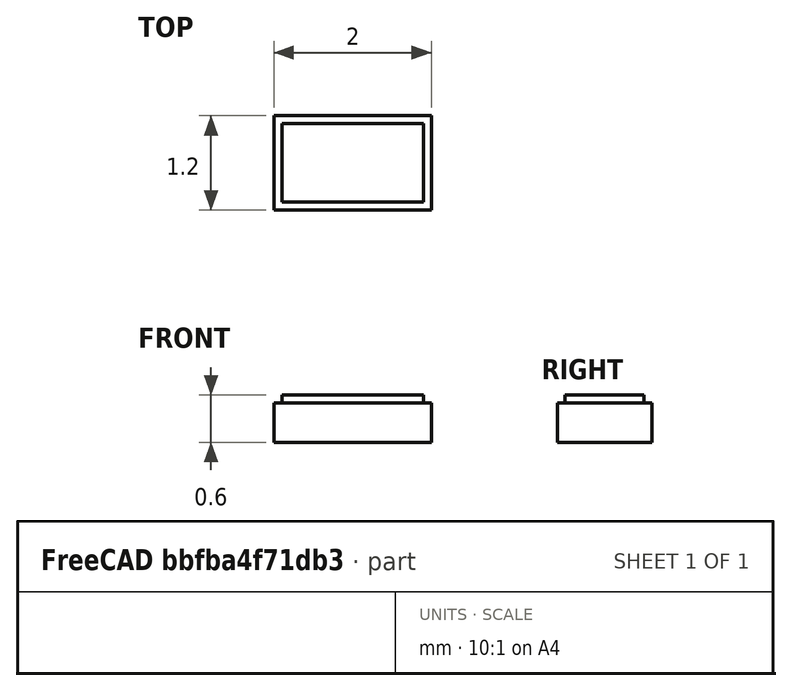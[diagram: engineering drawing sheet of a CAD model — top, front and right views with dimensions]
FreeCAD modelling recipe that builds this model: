
FCSTD DOCUMENT  (FreeCAD 0.16R6712 (Git))
Label: CRYSTAL-ABS06
License: All rights reserved
LicenseURL: http://en.wikipedia.org/wiki/All_rights_reserved
objects: Sketcher::SketchObject×2, PartDesign::Pad×2
note: 6 computed .brp shape members not serialized (recipe doc carries the construction recipe); baked Part::Feature solids carry a one-line shape summary decoded from their .brp

FEATURE [Sketcher::SketchObject] Sketch
  sketch-geometry (4):
    g0: LineSegment StartX=-1 StartY=0.6 StartZ=0 EndX=1 EndY=0.6 EndZ=0
    g1: LineSegment StartX=1 StartY=0.6 StartZ=0 EndX=1 EndY=-0.6 EndZ=0
    g2: LineSegment StartX=1 StartY=-0.6 StartZ=0 EndX=-1 EndY=-0.6 EndZ=0
    g3: LineSegment StartX=-1 StartY=-0.6 StartZ=0 EndX=-1 EndY=0.6 EndZ=0
  constraints (8):
    c: Coincident(g0,g1)
    c: Coincident(g1,g2)
    c: Coincident(g2,g3)
    c: Coincident(g3,g0)
    c: Horizontal(g0)
    c: Horizontal(g2)
    c: Vertical(g1)
    c: Vertical(g3)
FEATURE [PartDesign::Pad] Pad
  Length = 0.5
  Length2 = 100
  Sketch = -> Sketch
  Type = 0
FEATURE [Sketcher::SketchObject] Sketch001
  Placement = pos=(0,0,0.5) rot=(0,0,1;0rad)
  sketch-geometry (4):
    g0: LineSegment StartX=-0.9 StartY=0.5 StartZ=0 EndX=0.9 EndY=0.5 EndZ=0
    g1: LineSegment StartX=0.9 StartY=0.5 StartZ=0 EndX=0.9 EndY=-0.5 EndZ=0
    g2: LineSegment StartX=0.9 StartY=-0.5 StartZ=0 EndX=-0.9 EndY=-0.5 EndZ=0
    g3: LineSegment StartX=-0.9 StartY=-0.5 StartZ=0 EndX=-0.9 EndY=0.5 EndZ=0
  constraints (8):
    c: Coincident(g0,g1)
    c: Coincident(g1,g2)
    c: Coincident(g2,g3)
    c: Coincident(g3,g0)
    c: Horizontal(g0)
    c: Horizontal(g2)
    c: Vertical(g1)
    c: Vertical(g3)
FEATURE [PartDesign::Pad] Pad001
  Length = 0.1
  Length2 = 100
  Placement = pos=(0,0,0.5) rot=(0,0,1;0rad)
  Sketch = -> Sketch001
  Type = 0
